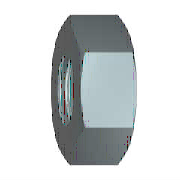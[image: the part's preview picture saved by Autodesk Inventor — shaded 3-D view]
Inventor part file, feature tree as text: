
AUTODESK INVENTOR PART (.ipt)
format: ipt  version: 2019 (Build 230136000, 136)  size: 162,816 bytes
history: native  units: mm (DEFAULTED — no unit token found)
features: sketch x3, extrude x1, chamfer x1, hole x1, other x1, plane x1
ambient origin geometry x7: Origin, YZ Plane, XZ Plane, X Axis, Y Axis, Z Axis, Center Point
bodies: Solid1 (feature_tree)
feature tree (8):
  extrude  "Cuerpo"  Depth=3.2mm
  chamfer  "Chaflán1"  Angle=30.0deg  [1 undecoded]
  hole  "Rosca"  [1 undecoded]
  other  "Work Axis1"
  plane  "Work Plane1"
  sketch  "Boceto1"  dims[d0=8.082904mm d1=3.2mm]
  sketch  "Boceto2"  dims[d2=0.0mm]
  sketch  "Boceto3"  dims[d3=30.0deg d4=30.0deg d5=5.9mm d6=5.9mm d7=90.0deg d25=3.242mm d26=6.0mm d27=4.0mm d28=2.0mm d29=14.3117mm d30=8.0mm d31=20.594885mm d8=0.378886mm d9=30.0deg d10=0.378886mm d11=30.0deg d13=0.0mm d14=0.0mm d39=0.0mm d40=0.378886mm d41=0.378886mm d42=0.0mm]
note: 2 required parameter values undecoded (feature->parameter linkage not recoverable at this tier; creation-order binding heuristic only, values carry confidence <= 0.55)
